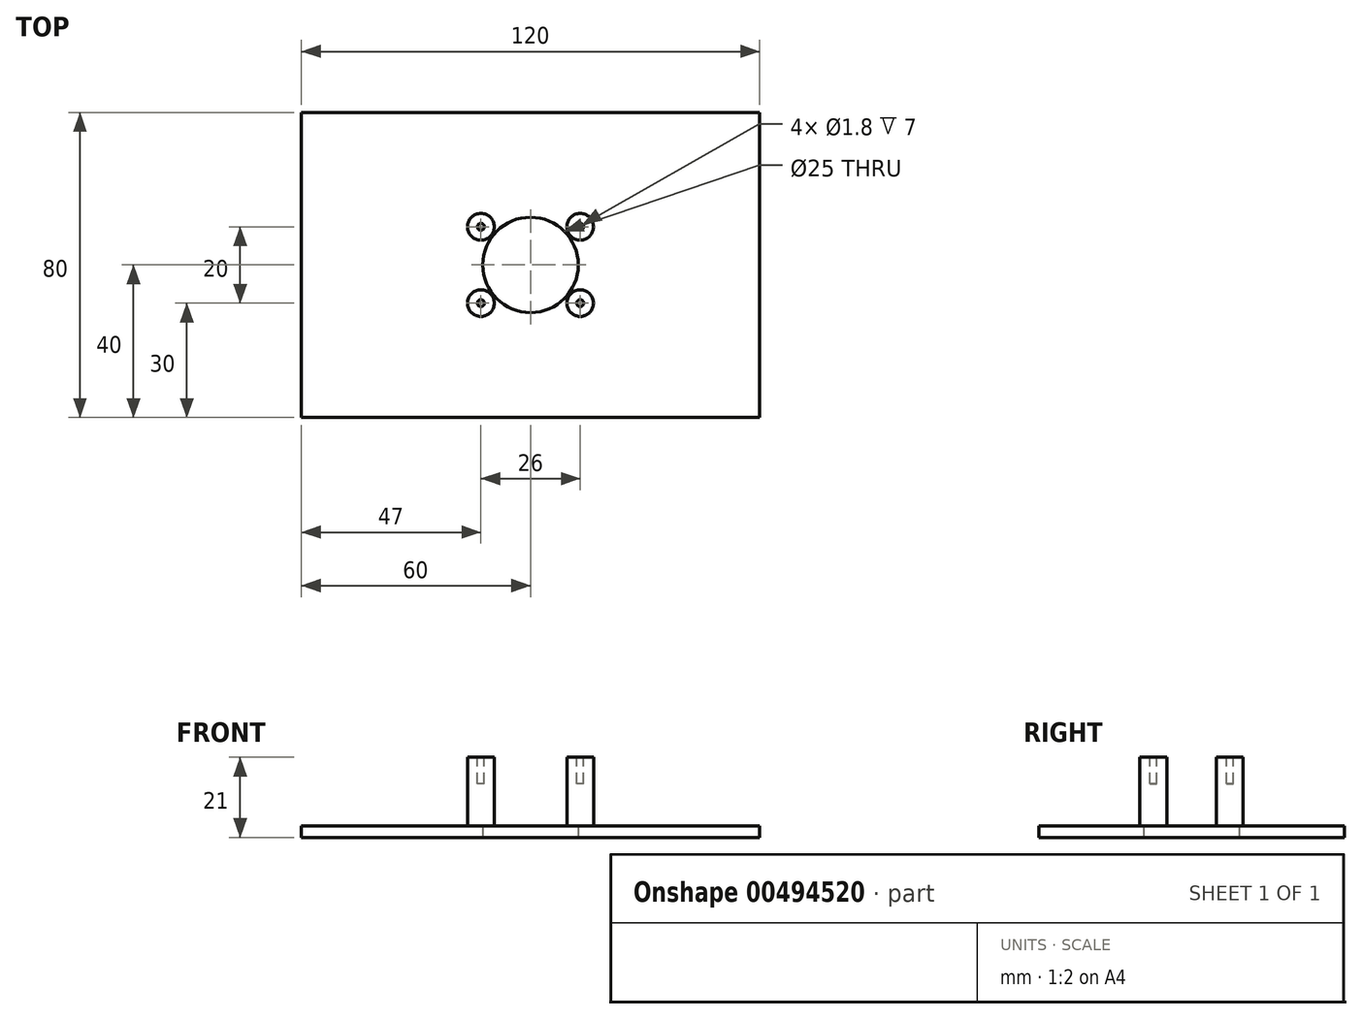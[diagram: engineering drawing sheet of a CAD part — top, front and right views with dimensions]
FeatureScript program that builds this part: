
annotation { "Feature Type Name" : "Feature", "Feature Type Description" : "" }
export const myFeature = defineFeature(function(context is Context, id is Id, definition is map)
    precondition{}
    {
        {
            var Q0;
            Q0=qCreatedBy(makeId("Top.planeOp"),FACE);
            var sketch = newSketch(context, id + "F0", { "sketchPlane" : qUnion([Q0])});
            skLineSegment(sketch, "E0.bottom", {"start": v(-60, 40) * mm, "end": v(60, 40) * mm});
            skLineSegment(sketch, "E0.top", {"start": v(-60, -40) * mm, "end": v(60, -40) * mm});
            skLineSegment(sketch, "E0.left", {"start": v(-60, 40) * mm, "end": v(-60, -40) * mm});
            skLineSegment(sketch, "E0.right", {"start": v(60, 40) * mm, "end": v(60, -40) * mm});
            skCircle(sketch, "E1", {"center": v(0, 0) * mm, "radius": 12.5 * mm});
            skSolve(sketch);
        }
        {
            var Q0;
            Q0=makeQuery(id+"F0.imprint","IMPRINT",FACE,{"disambiguationData":[TD([[makeQuery(id+"F0.imprint","IMPRINT",EDGE,{"derivedFrom":sQuery(id+"F0.wireOp",EDGE,"E0.bottom")}),-1.0]])]});
            extrude(context, id + "F1", {"entities" : qUnion([Q0]), "depth" : 3 * mm});
        }
        {
            var Q0;
            Q0=makeQuery(id+"F1.opExtrude","CAP_FACE",FACE,{"disambiguationData":[OSD([sQuery(id+"F0.wireOp",EDGE,"E0.bottom"),sQuery(id+"F0.wireOp",EDGE,"E0.top"),sQuery(id+"F0.wireOp",EDGE,"E0.left"),sQuery(id+"F0.wireOp",EDGE,"E0.right"),sQuery(id+"F0.wireOp",EDGE,"E1")])],"isStart":false});
            var sketch = newSketch(context, id + "F2", { "sketchPlane" : qUnion([Q0])});
            skCircle(sketch, "E2", {"center": v(13, 10) * mm, "radius": 3.5 * mm});
            skCircle(sketch, "E3", {"center": v(-13, 10) * mm, "radius": 3.5 * mm});
            skCircle(sketch, "E4", {"center": v(-13, -10) * mm, "radius": 3.5 * mm});
            skCircle(sketch, "E5", {"center": v(13, -10) * mm, "radius": 3.5 * mm});
            skSolve(sketch);
        }
        {
            var Q0;
            Q0=makeQuery(id+"F2.imprint","IMPRINT",FACE,{"disambiguationData":[TD([[makeQuery(id+"F2.imprint","IMPRINT",EDGE,{"derivedFrom":sQuery(id+"F2.wireOp",EDGE,"E3")}),1.0]])]});
            var Q1;
            Q1=makeQuery(id+"F2.imprint","IMPRINT",FACE,{"disambiguationData":[TD([[makeQuery(id+"F2.imprint","IMPRINT",EDGE,{"derivedFrom":sQuery(id+"F2.wireOp",EDGE,"E2")}),1.0]])]});
            var Q2;
            Q2=makeQuery(id+"F2.imprint","IMPRINT",FACE,{"disambiguationData":[TD([[makeQuery(id+"F2.imprint","IMPRINT",EDGE,{"derivedFrom":sQuery(id+"F2.wireOp",EDGE,"E5")}),1.0]])]});
            var Q3;
            Q3=makeQuery(id+"F2.imprint","IMPRINT",FACE,{"disambiguationData":[TD([[makeQuery(id+"F2.imprint","IMPRINT",EDGE,{"derivedFrom":sQuery(id+"F2.wireOp",EDGE,"E4")}),1.0]])]});
            extrude(context, id + "F3", {"entities" : qUnion([Q0, Q1, Q2, Q3]), "operationType" : NewBodyOperationType.ADD, "depth" : 18 * mm});
        }
        {
            var Q0;
            Q0=makeQuery(id+"F3.opExtrude","CAP_FACE",FACE,{"disambiguationData":[OSD([sQuery(id+"F2.wireOp",EDGE,"E4")])],"isStart":false});
            var sketch = newSketch(context, id + "F4", { "sketchPlane" : qUnion([Q0])});
            skCircle(sketch, "E6", {"center": v(-13, -10) * mm, "radius": 0.9 * mm});
            skCircle(sketch, "E7", {"center": v(-13, 10) * mm, "radius": 0.9 * mm});
            skCircle(sketch, "E8", {"center": v(13, 10) * mm, "radius": 0.9 * mm});
            skCircle(sketch, "E9", {"center": v(13, -10) * mm, "radius": 0.9 * mm});
            skSolve(sketch);
        }
        {
            var Q0;
            Q0=makeQuery(id+"F4.imprint","IMPRINT",FACE,{"disambiguationData":[TD([[makeQuery(id+"F4.imprint","IMPRINT",EDGE,{"derivedFrom":sQuery(id+"F4.wireOp",EDGE,"E7")}),1.0]])]});
            var Q1;
            Q1=makeQuery(id+"F4.imprint","IMPRINT",FACE,{"disambiguationData":[TD([[makeQuery(id+"F4.imprint","IMPRINT",EDGE,{"derivedFrom":sQuery(id+"F4.wireOp",EDGE,"E8")}),1.0]])]});
            var Q2;
            Q2=makeQuery(id+"F4.imprint","IMPRINT",FACE,{"disambiguationData":[TD([[makeQuery(id+"F4.imprint","IMPRINT",EDGE,{"derivedFrom":sQuery(id+"F4.wireOp",EDGE,"E9")}),1.0]])]});
            var Q3;
            Q3=makeQuery(id+"F4.imprint","IMPRINT",FACE,{"disambiguationData":[TD([[makeQuery(id+"F4.imprint","IMPRINT",EDGE,{"derivedFrom":sQuery(id+"F4.wireOp",EDGE,"E6")}),1.0]])]});
            extrude(context, id + "F5", {"entities" : qUnion([Q0, Q1, Q2, Q3]), "operationType" : NewBodyOperationType.REMOVE, "oppositeDirection" : true, "depth" : 7 * mm});
        }
    });
